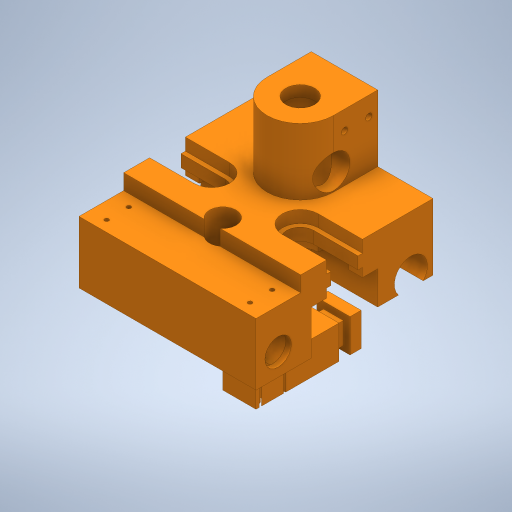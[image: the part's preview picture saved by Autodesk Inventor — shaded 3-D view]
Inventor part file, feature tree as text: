
AUTODESK INVENTOR PART (.ipt)
format: ipt  version: 2023 (Build 270158000, 158)  size: 672,256 bytes
history: native  units: mm
features: extrude x25, sketch x23, plane x3, mirror x2, other x1
ambient origin geometry x8: Origin, YZ Plane, XZ Plane, XY Plane, X Axis, Y Axis, Z Axis, Center Point
bodies: Solid1 (feature_tree)
feature tree (54):
  other  "<userpath>\OneDrive\ClawdDrive\Objet3D\3DPrinter\inventor\Parameters.xlsx"
  extrude  "Extrusion1"  Depth=80.0mm
  extrude  "Extrusion2"  Depth=40.0mm
  extrude  "Extrusion3"  Depth=20.0mm
  extrude  "Extrusion4"  Depth=16.2mm
  extrude  "Extrusion5"  Depth=5.5mm TaperAngle=0.0deg
  extrude  "Extrusion6"  Depth=4.0mm TaperAngle=0.0deg
  plane  "Work Plane1"
  mirror  "Mirror1"
  extrude  "Extrusion8"  Depth=8.1mm
  extrude  "Extrusion9"  Depth=25.0mm
  plane  "Work Plane2"
  mirror  "Mirror2"
  extrude  "Extrusion10"  Depth=15.0mm
  extrude  "Extrusion11"  Depth=15.0mm
  extrude  "Extrusion12"  Depth=5.0mm
  extrude  "Extrusion13"  Depth=80.0mm
  extrude  "Extrusion14"  Depth=15.0mm
  extrude  "Extrusion15"  Depth=10.0mm
  extrude  "Extrusion16"  Depth=20.2mm
  extrude  "Extrusion17"  TaperAngle=0.0deg  [1 undecoded]
  extrude  "Extrusion18"  Depth=1.9mm
  plane  "Work Plane3"
  extrude  "Extrusion20"  Depth=7.6mm
  extrude  "Extrusion21"  Depth=10.0mm
  extrude  "Extrusion22"  Depth=12.0mm
  extrude  "Extrusion23"  Depth=30.0mm
  extrude  "Extrusion24"  Depth=40.0mm
  extrude  "Extrusion25"  Depth=30.0mm TaperAngle=0.0deg
  extrude  "Extrusion26"  Depth=13.0mm
  extrude  "Extrusion27"  Depth=5.0mm TaperAngle=0.0deg
  sketch  "Sketch1"  dims[d0=80.0mm d1=80.0mm]
  sketch  "Sketch2"  dims[d2=15.0mm d3=0.0mm d7=40.0mm]
  sketch  "Sketch3"  dims[d8=20.0mm d9=12.2mm]
  sketch  "Sketch4"  dims[d10=10.0mm d11=0.0mm d12=16.2mm]
  sketch  "Sketch5"  dims[d13=4.0mm d14=0.0mm d15=5.5mm d16=0.0mm]
  sketch  "Sketch6"  dims[d17=13.8mm d18=4.0mm d19=0.0mm]
  sketch  "Sketch8"  dims[d20=16.2mm d21=8.1mm]
  sketch  "Sketch9"  dims[d22=25.0mm d23=25.0mm]
  sketch  "Sketch10"  dims[d24=15.0mm d25=15.0mm]
  sketch  "Sketch11"  dims[d29=15.0mm d32=15.0mm]
  sketch  "Sketch12"  dims[d33=5.0mm d34=5.0mm]
  sketch  "Sketch13"  dims[d35=80.0mm d36=0.0mm d37=0.0mm]
  sketch  "Sketch14"  dims[d38=15.0mm d39=15.0mm]
  sketch  "Sketch15"  dims[d40=60.0mm d41=10.0mm]
  sketch  "Sketch16"  dims[d42=10.0mm d49=20.2mm]
  sketch  "Sketch17"  dims[d50=7.0mm d51=0.0mm d52=0.0mm]
  sketch  "Sketch20"  dims[d53=1.9mm d54=1.9mm]
  sketch  "Sketch21"  dims[d55=7.6mm d56=7.6mm]
  sketch  "Sketch24"  dims[d57=10.0mm d58=4.9mm]
  sketch  "Sketch25"  dims[d59=10.0mm d60=0.0mm d61=12.0mm]
  sketch  "Sketch26"  dims[d62=20.0mm d63=0.0mm d64=30.0mm]
  sketch  "Sketch27"  dims[d65=20.0mm d66=40.0mm]
  sketch  "Sketch28"  dims[d67=20.0mm d68=30.0mm d69=0.0mm d70=13.0mm d71=5.0mm d72=0.0mm d73=35.0mm d74=0.0mm d75=2.9mm d76=2.9mm d77=11.0mm d78=4.0mm d79=8.5mm d80=8.5mm d81=15.0mm d82=0.0mm d83=6.0mm d84=15.0mm d85=8.0mm d86=17.0mm d87=0.0mm d88=15.0mm d89=0.0mm d90=32.5mm d91=15.0mm d92=15.0mm d93=32.5mm d94=45.0mm d95=0.0mm d96=7.5mm d97=7.5mm d98=15.0mm d99=32.5mm d100=0.0mm d101=-5.0mm d112=20.0mm d113=0.0mm d114=3.0mm d115=3.0mm d116=3.0mm d117=3.0mm d118=3.0mm d120=3.0mm d121=5.2mm d122=7.5mm d123=10.0mm d124=25.0mm d125=5.0mm d126=80.0mm d127=0.0mm d128=7.5mm d129=7.5mm d130=8.5mm d131=8.0mm d132=75.0mm d133=0.0mm d134=16.0mm d135=40.0mm d136=20.0mm d137=2.5mm d138=17.5mm d139=0.0mm d140=12.0mm d141=2.5mm d142=0.0mm d143=12.0mm d144=2.5mm d145=0.0mm d146=60.0mm d147=0.0mm d148=0.5mm d149=0.5mm d150=3.0mm d151=3.0mm d152=3.0mm d153=3.0mm d154=5.0mm d155=0.0mm d156=0.0mm]
note: 1 required parameter value undecoded (feature->parameter linkage not recoverable at this tier; creation-order binding heuristic only, values carry confidence <= 0.55)
